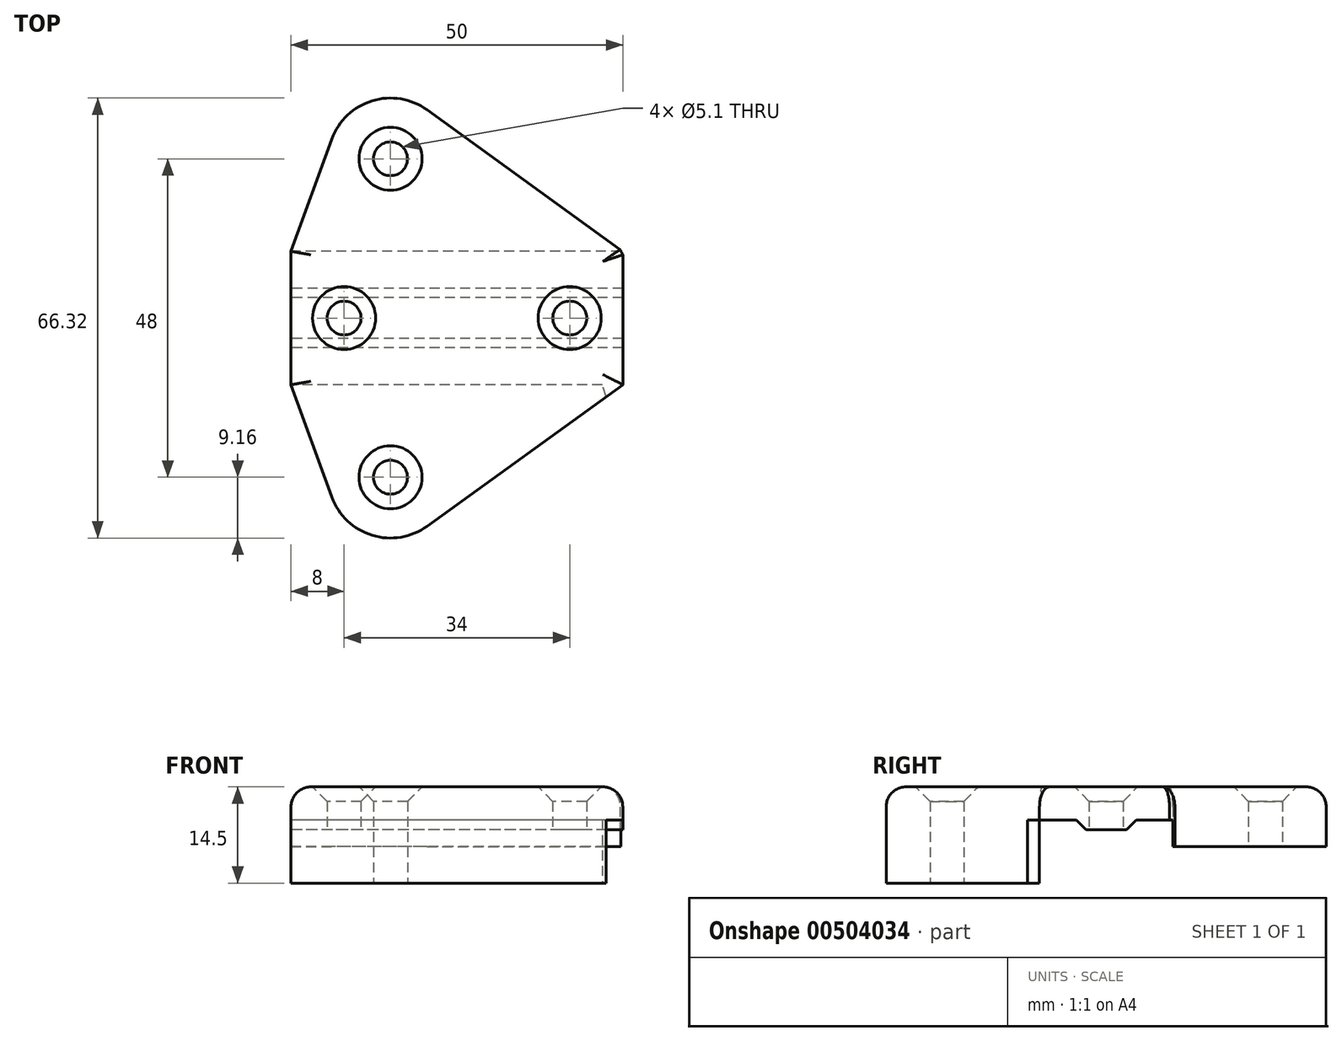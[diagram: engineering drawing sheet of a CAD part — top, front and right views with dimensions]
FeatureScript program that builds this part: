
annotation { "Feature Type Name" : "Feature", "Feature Type Description" : "" }
export const myFeature = defineFeature(function(context is Context, id is Id, definition is map)
    precondition{}
    {
        {
            var Q0;
            Q0=qCreatedBy(makeId("Top.planeOp"),FACE);
            var sketch = newSketch(context, id + "F0", { "sketchPlane" : qUnion([Q0])});
            skPoint(sketch, "E0.middle", {"position": v(0, 0) * mm});
            skLineSegment(sketch, "E1", {"start": v(-15, 10.05) * mm, "end": v(-8.84, 26.96) * mm});
            skLineSegment(sketch, "E2", {"start": v(0, 24) * mm, "end": v(0, -24) * mm, "construction": true});
            skCircle(sketch, "E3", {"center": v(-7, 0) * mm, "radius": 2.55 * mm});
            skLineSegment(sketch, "E4", {"start": v(-15, 10.05) * mm, "end": v(-15, -10.05) * mm});
            skLineSegment(sketch, "E5", {"start": v(-15, 0) * mm, "end": v(15, 0) * mm, "construction": true});
            skCircle(sketch, "E6", {"center": v(0, 24) * mm, "radius": 2.55 * mm});
            skCircle(sketch, "E7", {"center": v(0, -24) * mm, "radius": 2.55 * mm});
            skLineSegment(sketch, "E8", {"start": v(35, 10.05) * mm, "end": v(35, -10.05) * mm});
            skLineSegment(sketch, "E9", {"start": v(5.51, 31.37) * mm, "end": v(35, 10.05) * mm});
            skArc(sketch, "E10", {"start": v(5.51, 31.37) * mm, "mid": v(-2.76, 32.74) * mm, "end": v(-8.84, 26.96) * mm});
            skLineSegment(sketch, "E11.MirrorCS", {"start": v(5.51, -31.37) * mm, "end": v(35, -10.05) * mm});
            skArc(sketch, "E12.MirrorCS", {"start": v(5.51, -31.37) * mm, "mid": v(-2.76, -32.74) * mm, "end": v(-8.84, -26.96) * mm});
            skLineSegment(sketch, "E13.MirrorCS", {"start": v(-15, -10.05) * mm, "end": v(-8.84, -26.96) * mm});
            skCircle(sketch, "E14", {"center": v(27, 0) * mm, "radius": 2.55 * mm});
            skSolve(sketch);
        }
        {
            var Q0;
            Q0=makeQuery(id+"F0.imprint","IMPRINT",FACE,{"disambiguationData":[TD([[makeQuery(id+"F0.imprint","IMPRINT",EDGE,{"derivedFrom":sQuery(id+"F0.wireOp",EDGE,"E1")}),-1.0]])]});
            extrude(context, id + "F1", {"entities" : qUnion([Q0]), "depth" : 10 * mm, "offsetDistance" : 25 * mm});
        }
        {
            var Q0;
            Q0=makeQuery(id+"F1.opExtrude","SWEPT_FACE",FACE,{"disambiguationData":[OSD([sQuery(id+"F0.wireOp",EDGE,"E4")])]});
            var sketch = newSketch(context, id + "F2", { "sketchPlane" : qUnion([Q0])});
            skLineSegment(sketch, "E15", {"start": v(0, 0) * mm, "end": v(0, 10) * mm, "construction": true});
            skLineSegment(sketch, "E16.bottom", {"start": v(-10.05, 0) * mm, "end": v(10.05, 0) * mm});
            skLineSegment(sketch, "E16.top", {"start": v(-10.05, 5) * mm, "end": v(10.05, 5) * mm});
            skLineSegment(sketch, "E16.left", {"start": v(-10.05, 0) * mm, "end": v(-10.05, 5) * mm});
            skLineSegment(sketch, "E16.right", {"start": v(10.05, 0) * mm, "end": v(10.05, 5) * mm});
            skSolve(sketch);
        }
        {
            var Q0;
            Q0=makeQuery(id+"F2.imprint","IMPRINT",FACE,{"disambiguationData":[TD([[makeQuery(id+"F2.imprint","IMPRINT",EDGE,{"derivedFrom":sQuery(id+"F2.wireOp",EDGE,"E16.bottom")}),1.0]])]});
            extrude(context, id + "F3", {"entities" : qUnion([Q0]), "operationType" : NewBodyOperationType.REMOVE, "endBound" : BoundingType.THROUGH_ALL, "oppositeDirection" : true, "depth" : 25 * mm, "offsetDistance" : 25 * mm});
        }
        {
            var Q0;
            Q0=makeQuery(id+"F1.opExtrude","SWEPT_FACE",FACE,{"disambiguationData":[OSD([sQuery(id+"F0.wireOp",EDGE,"E4")])]});
            var sketch = newSketch(context, id + "F4", { "sketchPlane" : qUnion([Q0])});
            skLineSegment(sketch, "E17", {"start": v(4.5, 5) * mm, "end": v(3.05, 3.54) * mm});
            skLineSegment(sketch, "E18", {"start": v(3.05, 3.55) * mm, "end": v(-3.05, 3.55) * mm});
            skLineSegment(sketch, "E19", {"start": v(-3.05, 3.54) * mm, "end": v(-4.5, 5) * mm});
            skLineSegment(sketch, "E20", {"start": v(0, 10) * mm, "end": v(0, 5) * mm, "construction": true});
            skSolve(sketch);
        }
        {
            var Q0;
            {var subQ0=sQuery(id+"F4.wireOp",EDGE,"E17");Q0=makeQuery(id+"F4.imprint","IMPRINT",FACE,{"disambiguationData":[TD([[makeQuery(id+"F4.imprint","IMPRINT",EDGE,{"derivedFrom":subQ0}),-1.0]])]});}
            var Q1;
            Q1=makeQuery(id+"F1.opExtrude","SWEPT_FACE",FACE,{"disambiguationData":[OSD([sQuery(id+"F0.wireOp",EDGE,"E8")])]});
            extrude(context, id + "F5", {"entities" : qUnion([Q0]), "operationType" : NewBodyOperationType.ADD, "endBound" : BoundingType.UP_TO_SURFACE, "oppositeDirection" : true, "depth" : 25 * mm, "endBoundEntityFace" : qUnion([Q1]), "offsetDistance" : 25 * mm});
        }
        {
            var Q0;
            Q0=makeQuery(id+"F0.imprint","IMPRINT",FACE,{"disambiguationData":[TD([[makeQuery(id+"F0.imprint","IMPRINT",EDGE,{"derivedFrom":sQuery(id+"F0.wireOp",EDGE,"E3")}),1.0]])]});
            var Q1;
            Q1=makeQuery(id+"F0.imprint","IMPRINT",FACE,{"disambiguationData":[TD([[makeQuery(id+"F0.imprint","IMPRINT",EDGE,{"derivedFrom":sQuery(id+"F0.wireOp",EDGE,"E14")}),1.0]])]});
            var Q2;
            Q2=makeQuery(id+"F1.opExtrude","CAP_FACE",FACE,{"disambiguationData":[OSD([sQuery(id+"F0.wireOp",EDGE,"E0.left"),sQuery(id+"F0.wireOp",EDGE,"E0.right"),sQuery(id+"F0.wireOp",EDGE,"yQTNm3Th-nld5-GnkJ-OW5L-Ql5dlh6XEYzx"),sQuery(id+"F0.wireOp",EDGE,"pjTm0neV-uC3l-IQcS-6uSJ-sgK9bOUKop19"),sQuery(id+"F0.wireOp",EDGE,"E1"),sQuery(id+"F0.wireOp",EDGE,"rT5XyeMS-Sw6N-LAwE-mYcj-XK8ppVVwRFgd"),sQuery(id+"F0.wireOp",EDGE,"IMFvLOlx-2NYd-QAce-dW7n-0tB9ZtJLNvLB"),sQuery(id+"F0.wireOp",EDGE,"LDCHRpfb-Wy9b-yvqg-Pn7c-gEbTpYIF0iDg"),sQuery(id+"F0.wireOp",EDGE,"SBfZ0ZaC-sz1m-Xk8u-0noZ-aNedcS73Bl8m"),sQuery(id+"F0.wireOp",EDGE,"lhAWZnUN-VowD-uL3P-NqKj-8G4JGcrHoMbx")])],"isStart":false});
            extrude(context, id + "F6", {"entities" : qUnion([Q0, Q1]), "operationType" : NewBodyOperationType.REMOVE, "endBound" : BoundingType.UP_TO_SURFACE, "depth" : 25 * mm, "endBoundEntityFace" : qUnion([Q2]), "offsetDistance" : 25 * mm});
        }
        {
            var Q0;
            {var subQ0=sQuery(id+"F0.wireOp",EDGE,"E13.MirrorCS");var subQ1=sQuery(id+"F0.wireOp",EDGE,"E11.MirrorCS");var subQ2=sQuery(id+"F0.wireOp",EDGE,"E12.MirrorCS");var subQ3=sQuery(id+"F0.wireOp",EDGE,"E7");Q0=makeQuery(id+"F3.boolean.opBoolean","SPLIT",FACE,{"disambiguationData":[TD([makeQuery(id+"F1.opExtrude","SWEPT_FACE",FACE,{"disambiguationData":[OSD([subQ3])]})])],"derivedFrom":makeQuery(id+"F1.opExtrude","CAP_FACE",FACE,{"disambiguationData":[OSD([sQuery(id+"F0.wireOp",EDGE,"E1"),sQuery(id+"F0.wireOp",EDGE,"E3"),sQuery(id+"F0.wireOp",EDGE,"E4"),sQuery(id+"F0.wireOp",EDGE,"E6"),subQ3,sQuery(id+"F0.wireOp",EDGE,"E8"),sQuery(id+"F0.wireOp",EDGE,"E9"),sQuery(id+"F0.wireOp",EDGE,"E10"),subQ1,subQ2,subQ0,sQuery(id+"F0.wireOp",EDGE,"E14")])],"isStart":true})});}
            extrude(context, id + "F7", {"entities" : qUnion([Q0]), "operationType" : NewBodyOperationType.ADD, "depth" : 4.5 * mm, "offsetDistance" : 25 * mm});
        }
        {
            var Q0;
            {var subQ0=sQuery(id+"F0.wireOp",EDGE,"E10");var subQ1=sQuery(id+"F0.wireOp",EDGE,"E9");var subQ2=sQuery(id+"F0.wireOp",EDGE,"E6");var subQ3=sQuery(id+"F0.wireOp",EDGE,"E1");Q0=makeQuery(id+"F3.boolean.opBoolean","SPLIT",FACE,{"disambiguationData":[TD([makeQuery(id+"F1.opExtrude","SWEPT_FACE",FACE,{"disambiguationData":[OSD([subQ3])]})])],"derivedFrom":makeQuery(id+"F1.opExtrude","CAP_FACE",FACE,{"disambiguationData":[OSD([subQ3,sQuery(id+"F0.wireOp",EDGE,"E3"),sQuery(id+"F0.wireOp",EDGE,"E4"),subQ2,sQuery(id+"F0.wireOp",EDGE,"E7"),sQuery(id+"F0.wireOp",EDGE,"E8"),subQ1,subQ0,sQuery(id+"F0.wireOp",EDGE,"E11.MirrorCS"),sQuery(id+"F0.wireOp",EDGE,"E12.MirrorCS"),sQuery(id+"F0.wireOp",EDGE,"E13.MirrorCS"),sQuery(id+"F0.wireOp",EDGE,"E14")])],"isStart":true})});}
            extrude(context, id + "F8", {"entities" : qUnion([Q0]), "operationType" : NewBodyOperationType.REMOVE, "oppositeDirection" : true, "depth" : 1 * mm, "offsetDistance" : 25 * mm});
        }
        {
            var Q0;
            Q0=makeQuery(id+"F1.opExtrude","CAP_EDGE",EDGE,{"disambiguationData":[OSD([sQuery(id+"F0.wireOp",EDGE,"E1")])],"isStart":false});
            var Q1;
            Q1=makeQuery(id+"F1.opExtrude","CAP_EDGE",EDGE,{"disambiguationData":[OSD([sQuery(id+"F0.wireOp",EDGE,"SBfZ0ZaC-sz1m-Xk8u-0noZ-aNedcS73Bl8m")])],"isStart":false});
            var Q2;
            Q2=makeQuery(id+"F1.opExtrude","CAP_EDGE",EDGE,{"disambiguationData":[OSD([sQuery(id+"F0.wireOp",EDGE,"rT5XyeMS-Sw6N-LAwE-mYcj-XK8ppVVwRFgd")])],"isStart":false});
            var Q3;
            Q3=makeQuery(id+"F1.opExtrude","CAP_EDGE",EDGE,{"disambiguationData":[OSD([sQuery(id+"F0.wireOp",EDGE,"E0.left")])],"isStart":false});
            var Q4;
            Q4=makeQuery(id+"F1.opExtrude","CAP_EDGE",EDGE,{"disambiguationData":[OSD([sQuery(id+"F0.wireOp",EDGE,"LDCHRpfb-Wy9b-yvqg-Pn7c-gEbTpYIF0iDg")])],"isStart":false});
            var Q5;
            Q5=makeQuery(id+"F1.opExtrude","CAP_EDGE",EDGE,{"disambiguationData":[OSD([sQuery(id+"F0.wireOp",EDGE,"lhAWZnUN-VowD-uL3P-NqKj-8G4JGcrHoMbx")])],"isStart":false});
            var Q6;
            Q6=makeQuery(id+"F1.opExtrude","CAP_EDGE",EDGE,{"disambiguationData":[OSD([sQuery(id+"F0.wireOp",EDGE,"IMFvLOlx-2NYd-QAce-dW7n-0tB9ZtJLNvLB")])],"isStart":false});
            var Q7;
            Q7=makeQuery(id+"F1.opExtrude","CAP_EDGE",EDGE,{"disambiguationData":[OSD([sQuery(id+"F0.wireOp",EDGE,"E0.right")])],"isStart":false});
            var Q8;
            Q8=makeQuery(id+"F1.opExtrude","CAP_EDGE",EDGE,{"disambiguationData":[OSD([sQuery(id+"F0.wireOp",EDGE,"68wsDqlh-E97Z-fuaE-rq3D-OJhXVWCGhKqR")])],"isStart":false});
            var Q9;
            Q9=makeQuery(id+"F1.opExtrude","CAP_EDGE",EDGE,{"disambiguationData":[OSD([sQuery(id+"F0.wireOp",EDGE,"E4")])],"isStart":false});
            var Q10;
            Q10=makeQuery(id+"F1.opExtrude","CAP_EDGE",EDGE,{"disambiguationData":[OSD([sQuery(id+"F0.wireOp",EDGE,"E13.MirrorCS")])],"isStart":false});
            var Q11;
            Q11=makeQuery(id+"F1.opExtrude","CAP_EDGE",EDGE,{"disambiguationData":[OSD([sQuery(id+"F0.wireOp",EDGE,"E8")])],"isStart":false});
            fillet(context, id + "F9", {"entities" : qUnion([Q0, Q1, Q2, Q3, Q4, Q5, Q6, Q7, Q8, Q9, Q10, Q11]), "radius" : 3 * mm, "tangentPropagation" : true, "allowEdgeOverflow" : false});
        }
        {
            var Q0;
            Q0=makeQuery(id+"F1.opExtrude","CAP_EDGE",EDGE,{"disambiguationData":[OSD([sQuery(id+"F0.wireOp",EDGE,"E7")])],"isStart":false});
            var Q1;
            Q1=makeQuery(id+"F1.opExtrude","CAP_EDGE",EDGE,{"disambiguationData":[OSD([sQuery(id+"F0.wireOp",EDGE,"E3")])],"isStart":false});
            var Q2;
            Q2=makeQuery(id+"F1.opExtrude","CAP_EDGE",EDGE,{"disambiguationData":[OSD([sQuery(id+"F0.wireOp",EDGE,"E6")])],"isStart":false});
            var Q3;
            Q3=makeQuery(id+"F1.opExtrude","CAP_EDGE",EDGE,{"disambiguationData":[OSD([sQuery(id+"F0.wireOp",EDGE,"E14")])],"isStart":false});
            chamfer(context, id + "F10", {"entities" : qUnion([Q0, Q1, Q2, Q3]), "width" : 2.2 * mm, "tangentPropagation" : true});
        }
        {
            var Q0;
            {var subQ0=sQuery(id+"F0.wireOp",EDGE,"E9");Q0=makeQuery(id+"F3.boolean.opBoolean","SPLIT",EDGE,{"disambiguationData":[topologyDisambiguationEdgeConnected([makeQuery(id+"F3.opExtrude","SWEPT_FACE",FACE,{"disambiguationData":[OSD([sQuery(id+"F2.wireOp",EDGE,"E16.left")])]})])],"derivedFrom":makeQuery(id+"F1.opExtrude","SWEPT_EDGE",EDGE,{"disambiguationData":[OSD([sQuery(id+"F0.wireOp",EDGE,"E8"),subQ0])]})});}
            var Q1;
            {var subQ0=sQuery(id+"F0.wireOp",EDGE,"E11.MirrorCS");var subQ1=sQuery(id+"F0.wireOp",EDGE,"E8");Q1=makeQuery(id+"F7.boolean.opBoolean","MERGE",EDGE,{"derivedFrom":[makeQuery(id+"F3.boolean.opBoolean","SPLIT",EDGE,{"disambiguationData":[topologyDisambiguationEdgeConnected([makeQuery(id+"F3.opExtrude","SWEPT_FACE",FACE,{"disambiguationData":[OSD([sQuery(id+"F2.wireOp",EDGE,"E16.right")])]})])],"derivedFrom":makeQuery(id+"F1.opExtrude","SWEPT_EDGE",EDGE,{"disambiguationData":[OSD([subQ1,subQ0])]})}),makeQuery(id+"F7.opExtrude","SWEPT_EDGE",EDGE,{"disambiguationData":[OSD([subQ1,subQ0])]})]});}
            chamfer(context, id + "F11", {"entities" : qUnion([Q0, Q1]), "width" : 1 * mm, "tangentPropagation" : true});
        }
    });
